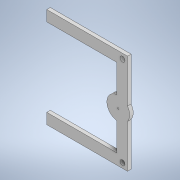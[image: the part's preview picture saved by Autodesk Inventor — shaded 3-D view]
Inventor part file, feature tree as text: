
AUTODESK INVENTOR PART (.ipt)
format: ipt  version: 2022 (Build 260153000, 153)  size: 115,200 bytes
history: native  units: mm
features: other x1, extrude x1, sketch x1
ambient origin geometry x8: Origin, YZ Plane, XZ Plane, XY Plane, X Axis, Y Axis, Z Axis, Center Point
bodies: Body1 (feature_tree)
feature tree (3):
  other  "Sólido1"
  extrude  "Extrusión1"  Depth=5.0mm TaperAngle=0.0deg
  sketch  "Boceto1"  dims[d0=2.0mm d1=5.0mm d2=0.0mm]
